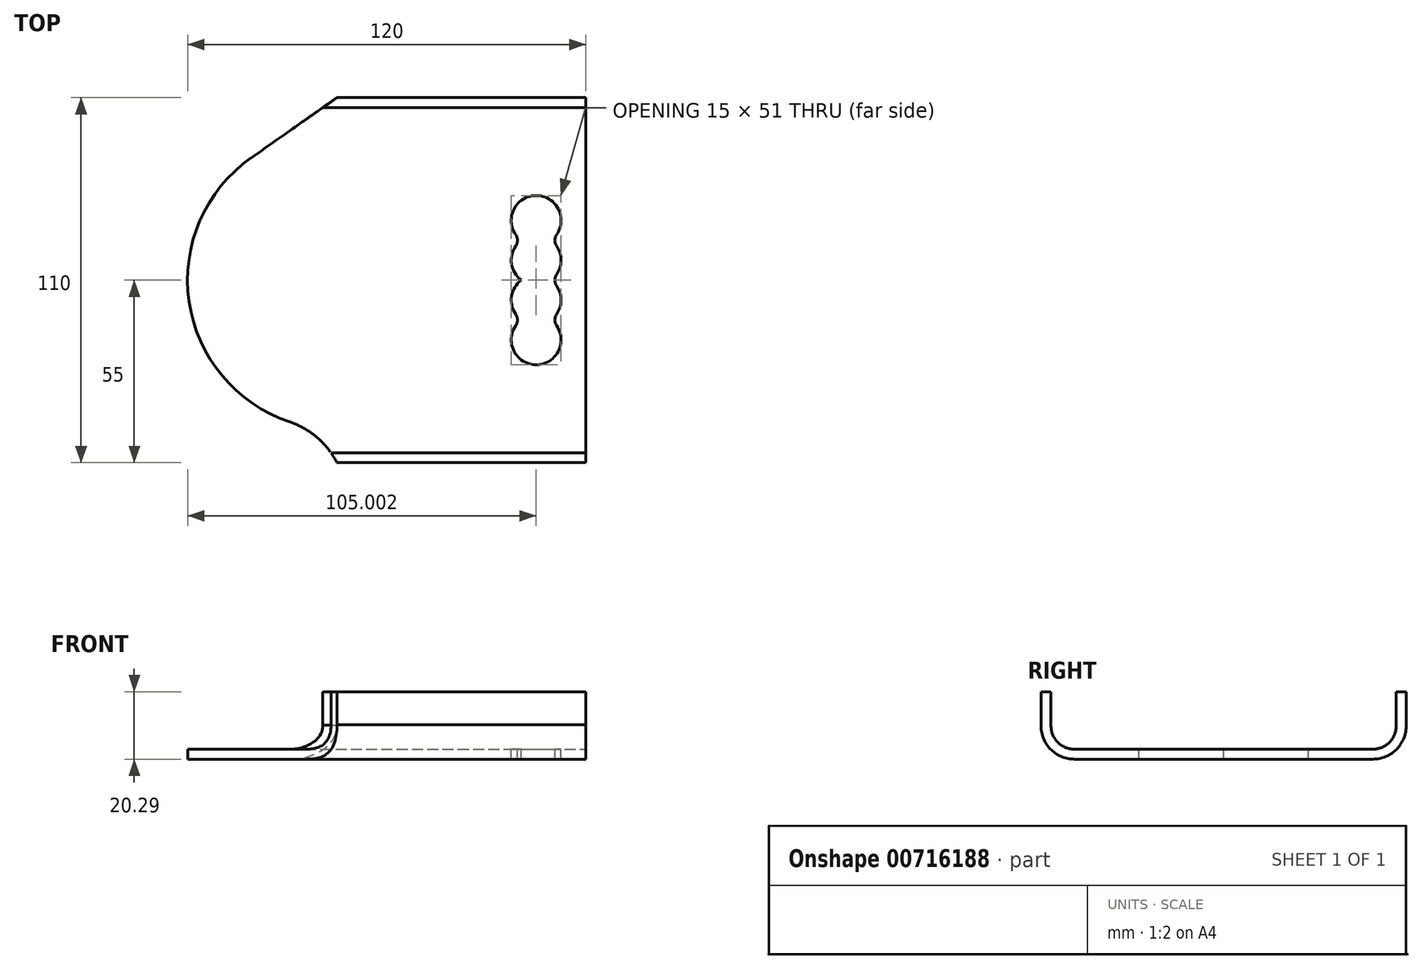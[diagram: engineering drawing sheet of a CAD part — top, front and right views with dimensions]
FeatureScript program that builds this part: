
annotation { "Feature Type Name" : "Feature", "Feature Type Description" : "" }
export const myFeature = defineFeature(function(context is Context, id is Id, definition is map)
    precondition{}
    {
        {
            var Q0;
            Q0=qCreatedBy(makeId("Top.planeOp"),FACE);
            var sketch = newSketch(context, id + "F0", { "sketchPlane" : qUnion([Q0])});
            skPoint(sketch, "E0.middle", {"position": v(0, 0) * mm});
            skLineSegment(sketch, "E1.bottom", {"start": v(0, 0) * mm, "end": v(120, 0) * mm});
            skLineSegment(sketch, "E1.top", {"start": v(45, -45) * mm, "end": v(120, -45) * mm});
            skLineSegment(sketch, "E1.right", {"start": v(120, 0) * mm, "end": v(120, -45) * mm});
            skArc(sketch, "E2", {"start": v(45, -45) * mm, "mid": v(13.18, -31.82) * mm, "end": v(0, 0) * mm});
            skSolve(sketch);
        }
        {
            var Q0;
            Q0 = qSketchRegion(id + "F0", true);
            extrude(context, id + "F1", {"entities" : qUnion([Q0]), "depth" : 3 * mm, "offsetDistance" : 25 * mm});
        }
        {
            var Q0;
            Q0 = qSketchRegion(id + "F0", true);
            extrude(context, id + "F2", {"entities" : qUnion([Q0]), "operationType" : NewBodyOperationType.ADD, "depth" : 3 * mm, "offsetDistance" : 25 * mm});
        }
        {
            var Q0;
            Q0=makeQuery(id+"F1.opExtrude","SWEPT_FACE",FACE,{"disambiguationData":[OSD([sQuery(id+"F0.wireOp",EDGE,"E1.right")])]});
            var sketch = newSketch(context, id + "F3", { "sketchPlane" : qUnion([Q0])});
            skArc(sketch, "E3", {"start": v(-55, 10.3) * mm, "mid": v(-52.17, 3.03) * mm, "end": v(-45, 0) * mm});
            skArc(sketch, "E4.0", {"start": v(-52, 10.2) * mm, "mid": v(-50.02, 5.12) * mm, "end": v(-45, 3) * mm});
            skLineSegment(sketch, "E5", {"start": v(-55, 10.3) * mm, "end": v(-55, 20.3) * mm});
            skLineSegment(sketch, "E6", {"start": v(-55, 20.3) * mm, "end": v(-52, 20.3) * mm});
            skLineSegment(sketch, "E7", {"start": v(-52, 20.3) * mm, "end": v(-52, 10.2) * mm});
            skLineSegment(sketch, "E8", {"start": v(-45, 0) * mm, "end": v(-45, 3) * mm});
            skSolve(sketch);
        }
        {
            var Q0;
            Q0 = qSketchRegion(id + "F3", true);
            extrude(context, id + "F4", {"entities" : qUnion([Q0]), "operationType" : NewBodyOperationType.ADD, "oppositeDirection" : true, "depth" : 75 * mm, "offsetDistance" : 25 * mm});
        }
        {
            var Q0;
            Q0=makeQuery(id+"F1.opExtrude","CAP_FACE",FACE,{"disambiguationData":[OSD([sQuery(id+"F0.wireOp",EDGE,"E1.bottom"),sQuery(id+"F0.wireOp",EDGE,"E1.top"),sQuery(id+"F0.wireOp",EDGE,"E1.right"),sQuery(id+"F0.wireOp",EDGE,"E2")])],"isStart":false});
            var sketch = newSketch(context, id + "F5", { "sketchPlane" : qUnion([Q0])});
            skArc(sketch, "E9", {"start": v(100.5, -12) * mm, "mid": v(105, -25.5) * mm, "end": v(109.5, -12) * mm});
            skArc(sketch, "E10", {"start": v(109.5, -12) * mm, "mid": v(112.5, -6) * mm, "end": v(109.5, 0) * mm});
            skLineSegment(sketch, "E11", {"start": v(100.5, 0) * mm, "end": v(109.5, 0) * mm});
            skArc(sketch, "E12.trimOffspring", {"start": v(100.5, 0) * mm, "mid": v(97.5, -6) * mm, "end": v(100.5, -12) * mm});
            skSolve(sketch);
        }
        {
            var Q0;
            Q0=makeQuery(id+"F5.imprint","IMPRINT",FACE,{"disambiguationData":[TD([[makeQuery(id+"F5.imprint","IMPRINT",EDGE,{"derivedFrom":sQuery(id+"F5.wireOp",EDGE,"E9")}),1.0]])]});
            extrude(context, id + "F6", {"entities" : qUnion([Q0]), "operationType" : NewBodyOperationType.REMOVE, "oppositeDirection" : true, "depth" : 25 * mm, "offsetDistance" : 25 * mm});
        }
        {
            var Q0;
            Q0=makeQuery(id+"F1.opExtrude","SWEPT_BODY",BODY,{"disambiguationData":[OSD([sQuery(id+"F0.wireOp",EDGE,"E1.bottom"),sQuery(id+"F0.wireOp",EDGE,"E1.top"),sQuery(id+"F0.wireOp",EDGE,"E1.right"),sQuery(id+"F0.wireOp",EDGE,"E2")])]});
            var Q1;
            Q1=qCreatedBy(makeId("Front.planeOp"),FACE);
            mirror(context, id + "F7", {"operationType" : NewBodyOperationType.ADD, "entities" : qUnion([Q0]), "mirrorPlane" : qUnion([Q1])});
        }
        {
            var Q0;
            {var subQ0=makeQuery(id+"F6.boolean.opBoolean","COPY",EDGE,{"derivedFrom":makeQuery(id+"F6.opExtrude","SWEPT_EDGE",EDGE,{"disambiguationData":[OSD([sQuery(id+"F0.wireOp",EDGE,"E1.bottom"),sQuery(id+"F5.wireOp",EDGE,"E11"),sQuery(id+"F5.wireOp",EDGE,"E12.trimOffspring")])]})});Q0=makeQuery(id+"F7.boolean.opBoolean","MERGE",EDGE,{"derivedFrom":[subQ0,makeQuery(id+"F7.opPattern","COPY",EDGE,{"derivedFrom":subQ0,"instanceName":"1"})]});}
            var Q1;
            Q1=makeQuery(id+"F6.boolean.opBoolean","COPY",EDGE,{"derivedFrom":makeQuery(id+"F6.opExtrude","SWEPT_EDGE",EDGE,{"disambiguationData":[OSD([sQuery(id+"F5.wireOp",EDGE,"E9"),sQuery(id+"F5.wireOp",EDGE,"E12.trimOffspring")])]})});
            var Q2;
            Q2=makeQuery(id+"F7.opPattern","COPY",EDGE,{"derivedFrom":makeQuery(id+"F6.boolean.opBoolean","COPY",EDGE,{"derivedFrom":makeQuery(id+"F6.opExtrude","SWEPT_EDGE",EDGE,{"disambiguationData":[OSD([sQuery(id+"F5.wireOp",EDGE,"E9"),sQuery(id+"F5.wireOp",EDGE,"E12.trimOffspring")])]})}),"instanceName":"1"});
            var Q3;
            Q3=makeQuery(id+"F6.boolean.opBoolean","COPY",EDGE,{"derivedFrom":makeQuery(id+"F6.opExtrude","SWEPT_EDGE",EDGE,{"disambiguationData":[OSD([sQuery(id+"F5.wireOp",EDGE,"E9"),sQuery(id+"F5.wireOp",EDGE,"E10")])]})});
            var Q4;
            {var subQ0=makeQuery(id+"F6.boolean.opBoolean","COPY",EDGE,{"derivedFrom":makeQuery(id+"F6.opExtrude","SWEPT_EDGE",EDGE,{"disambiguationData":[OSD([sQuery(id+"F0.wireOp",EDGE,"E1.bottom"),sQuery(id+"F5.wireOp",EDGE,"E10"),sQuery(id+"F5.wireOp",EDGE,"E11")])]})});Q4=makeQuery(id+"F7.boolean.opBoolean","MERGE",EDGE,{"derivedFrom":[subQ0,makeQuery(id+"F7.opPattern","COPY",EDGE,{"derivedFrom":subQ0,"instanceName":"1"})]});}
            var Q5;
            Q5=makeQuery(id+"F7.opPattern","COPY",EDGE,{"derivedFrom":makeQuery(id+"F6.boolean.opBoolean","COPY",EDGE,{"derivedFrom":makeQuery(id+"F6.opExtrude","SWEPT_EDGE",EDGE,{"disambiguationData":[OSD([sQuery(id+"F5.wireOp",EDGE,"E9"),sQuery(id+"F5.wireOp",EDGE,"E10")])]})}),"instanceName":"1"});
            fillet(context, id + "F8", {"entities" : qUnion([Q0, Q1, Q2, Q3, Q4, Q5]), "radius" : 3 * mm, "tangentPropagation" : true, "allowEdgeOverflow" : false});
        }
        {
            var Q0;
            Q0=makeQuery(id+"F7.opPattern","COPY",EDGE,{"derivedFrom":makeQuery(id+"F4.boolean.opBoolean","MERGE",EDGE,{"derivedFrom":[makeQuery(id+"F1.opExtrude","SWEPT_EDGE",EDGE,{"disambiguationData":[OSD([sQuery(id+"F0.wireOp",EDGE,"E1.top"),sQuery(id+"F0.wireOp",EDGE,"E2")])]}),makeQuery(id+"F4.opExtrude","CAP_EDGE",EDGE,{"disambiguationData":[OSD([sQuery(id+"F3.wireOp",EDGE,"E8")])],"isStart":false})]}),"instanceName":"1"});
            fillet(context, id + "F9", {"entities" : qUnion([Q0]), "radius" : 25000 * mm, "tangentPropagation" : true, "allowEdgeOverflow" : false});
        }
        {
            var Q0;
            Q0=makeQuery(id+"F4.boolean.opBoolean","MERGE",EDGE,{"derivedFrom":[makeQuery(id+"F1.opExtrude","SWEPT_EDGE",EDGE,{"disambiguationData":[OSD([sQuery(id+"F0.wireOp",EDGE,"E1.top"),sQuery(id+"F0.wireOp",EDGE,"E2")])]}),makeQuery(id+"F4.opExtrude","CAP_EDGE",EDGE,{"disambiguationData":[OSD([sQuery(id+"F3.wireOp",EDGE,"E8")])],"isStart":false})]});
            fillet(context, id + "F10", {"entities" : qUnion([Q0]), "radius" : 25 * mm, "tangentPropagation" : true, "allowEdgeOverflow" : false});
        }
    });
